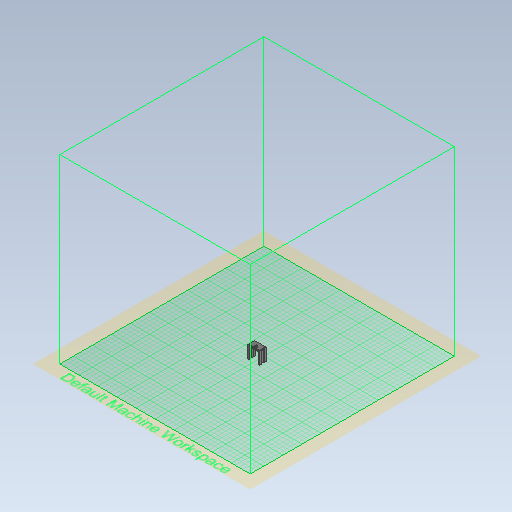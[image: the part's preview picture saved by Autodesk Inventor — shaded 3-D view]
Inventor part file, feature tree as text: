
AUTODESK INVENTOR PART (.ipt)
format: ipt  version: 2020 (Build 240168000, 168)  size: 547,328 bytes
history: native  units: mm
features: extrude x10, projected_geometry x7, sketch x5, fillet x4
ambient origin geometry x8: Origin, YZ Plane, XZ Plane, XY Plane, X Axis, Y Axis, Z Axis, Center Point
bodies: Body1 (feature_tree)
feature tree (26):
  extrude  "Выдавливание7"  Depth=4.0mm
  extrude  "Выдавливание16"  Depth=25.5mm
  sketch  "Эскиз12"
  extrude  "Выдавливание17"  Depth=3.0mm
  extrude  "Выдавливание18"  Depth=3.0mm
  extrude  "Выдавливание19"  Depth=3.0mm
  fillet  "Сопряжение1"  Radius=20.2mm
  extrude  "Выдавливание20"  Depth=14.0mm TaperAngle=0.0deg
  fillet  "Сопряжение2"  Radius=26.0mm
  extrude  "Выдавливание21"  Depth=20.5mm
  extrude  "Выдавливание22"  Depth=3.0mm
  extrude  "Выдавливание23"  Depth=1.5mm
  extrude  "Выдавливание24"  Depth=0.5mm
  fillet  "Сопряжение3"  Radius=0.5mm
  fillet  "Сопряжение4"  Radius=0.5mm
  sketch  "Эскиз1"
  sketch  "Эскиз10"
  projected_geometry  "Спроецированная петля9"
  projected_geometry  "Спроецированная петля10"
  projected_geometry  "Спроецированная петля11"
  projected_geometry  "Спроецированная петля12"
  projected_geometry  "Спроецированная петля13"
  sketch  "Эскиз14"
  projected_geometry  "Спроецированная петля15"
  sketch  "Эскиз16"
  projected_geometry  "Спроецированная петля16"
